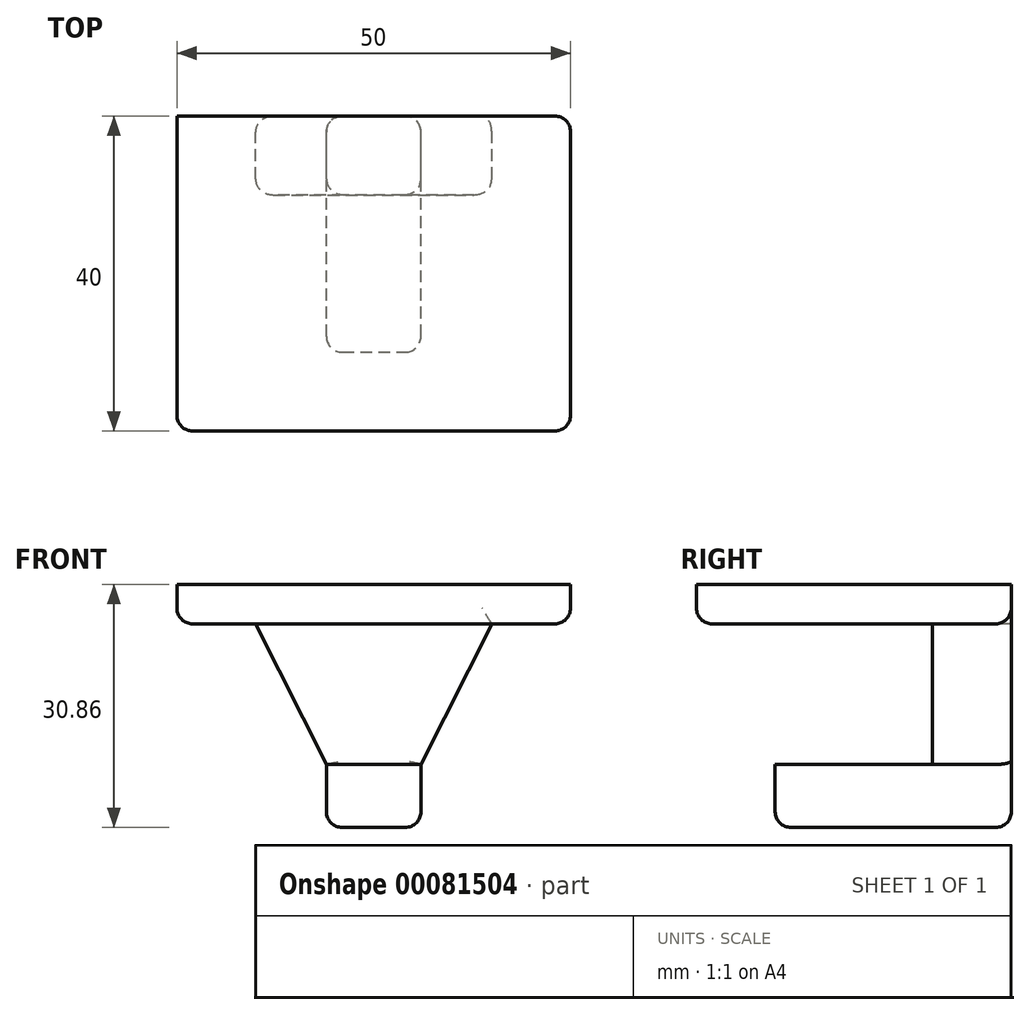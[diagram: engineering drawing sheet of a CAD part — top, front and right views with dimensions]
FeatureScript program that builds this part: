
annotation { "Feature Type Name" : "Feature", "Feature Type Description" : "" }
export const myFeature = defineFeature(function(context is Context, id is Id, definition is map)
    precondition{}
    {
        {
            var Q0;
            Q0=qCreatedBy(makeId("Front.planeOp"),FACE);
            var sketch = newSketch(context, id + "F0", { "sketchPlane" : qUnion([Q0])});
            skLineSegment(sketch, "E0.bottom", {"start": v(-25, 42.41) * mm, "end": v(25, 42.41) * mm});
            skLineSegment(sketch, "E0.top", {"start": v(-25, 37.41) * mm, "end": v(25, 37.41) * mm});
            skLineSegment(sketch, "E0.left", {"start": v(-25, 42.41) * mm, "end": v(-25, 37.41) * mm});
            skLineSegment(sketch, "E0.right", {"start": v(25, 42.41) * mm, "end": v(25, 37.41) * mm});
            skPoint(sketch, "E0.middle", {"position": v(0, 39.91) * mm});
            skLineSegment(sketch, "E1.bottom", {"start": v(-6, 19.55) * mm, "end": v(6, 19.55) * mm});
            skLineSegment(sketch, "E1.top", {"start": v(-6, 11.55) * mm, "end": v(6, 11.55) * mm});
            skLineSegment(sketch, "E1.left", {"start": v(-6, 19.55) * mm, "end": v(-6, 11.55) * mm});
            skLineSegment(sketch, "E1.right", {"start": v(6, 19.55) * mm, "end": v(6, 11.55) * mm});
            skPoint(sketch, "E1.middle", {"position": v(0, 15.55) * mm});
            skLineSegment(sketch, "E2", {"start": v(-15, 37.41) * mm, "end": v(-6, 19.55) * mm});
            skLineSegment(sketch, "E3", {"start": v(15, 37.41) * mm, "end": v(6, 19.55) * mm});
            skSolve(sketch);
        }
        {
            var Q0;
            Q0=makeQuery(id+"F0.imprint","IMPRINT",FACE,{"disambiguationData":[TD([[makeQuery(id+"F0.imprint","IMPRINT",EDGE,{"derivedFrom":sQuery(id+"F0.wireOp",EDGE,"E0.bottom")}),-1.0]])]});
            var Q1;
            Q1=makeQuery(id+"F0.imprint","IMPRINT",FACE,{"disambiguationData":[TD([[makeQuery(id+"F0.imprint","IMPRINT",EDGE,{"derivedFrom":sQuery(id+"F0.wireOp",EDGE,"E1.bottom")}),-1.0]])]});
            extrude(context, id + "F1", {"entities" : qUnion([Q0, Q1]), "depth" : 30 * mm});
        }
        {
            var Q0;
            Q0=makeQuery(id+"F1.opExtrude","CAP_FACE",FACE,{"disambiguationData":[OSD([sQuery(id+"F0.wireOp",EDGE,"E0.bottom"),sQuery(id+"F0.wireOp",EDGE,"E0.top"),sQuery(id+"F0.wireOp",EDGE,"E0.left"),sQuery(id+"F0.wireOp",EDGE,"E0.right")])],"isStart":false});
            extrude(context, id + "F2", {"entities" : qUnion([Q0]), "operationType" : NewBodyOperationType.ADD, "depth" : 10 * mm});
        }
        {
            var Q0;
            Q0=qCreatedBy(makeId("Front.planeOp"),FACE);
            var sketch = newSketch(context, id + "F3", { "sketchPlane" : qUnion([Q0])});
            skLineSegment(sketch, "E4", {"start": v(-6, 19.55) * mm, "end": v(-15, 37.41) * mm});
            skLineSegment(sketch, "E5", {"start": v(-15, 37.41) * mm, "end": v(15, 37.41) * mm});
            skLineSegment(sketch, "E6", {"start": v(15, 37.41) * mm, "end": v(6, 19.55) * mm});
            skLineSegment(sketch, "E7", {"start": v(6, 19.55) * mm, "end": v(-6, 19.55) * mm});
            skSolve(sketch);
        }
        {
            var Q0;
            Q0=sQuery(id+"F3.wireOp",EDGE,"E6");
            var Q1;
            Q1=sQuery(id+"F3.wireOp",EDGE,"E7");
            var Q2;
            Q2=sQuery(id+"F3.wireOp",EDGE,"E5");
            var Q3;
            Q3=sQuery(id+"F3.wireOp",EDGE,"E4");
            extrude(context, id + "F4", {"bodyType" : ToolBodyType.SURFACE, "surfaceEntities" : qUnion([Q0, Q1, Q2, Q3]), "depth" : 10 * mm});
        }
        {
            var Q0;
            Q0 = qSketchRegion(id + "F3", true);
            extrude(context, id + "F5", {"entities" : qUnion([Q0]), "depth" : 10 * mm});
        }
        {
            var Q0;
            {var subQ0=sQuery(id+"F0.wireOp",EDGE,"E0.left");var subQ1=sQuery(id+"F0.wireOp",EDGE,"E0.top");Q0=makeQuery(id+"F2.boolean.opBoolean","MERGE",EDGE,{"derivedFrom":[makeQuery(id+"F1.opExtrude","SWEPT_EDGE",EDGE,{"disambiguationData":[OSD([subQ1,subQ0])]}),makeQuery(id+"F2.opExtrude","SWEPT_EDGE",EDGE,{"disambiguationData":[OSD([subQ1,subQ0])]})]});}
            var Q1;
            Q1=makeQuery(id+"F2.opExtrude","CAP_EDGE",EDGE,{"disambiguationData":[OSD([sQuery(id+"F0.wireOp",EDGE,"E0.top")])],"isStart":false});
            var Q2;
            {var subQ0=sQuery(id+"F0.wireOp",EDGE,"E0.right");var subQ1=sQuery(id+"F0.wireOp",EDGE,"E0.top");Q2=makeQuery(id+"F2.boolean.opBoolean","MERGE",EDGE,{"derivedFrom":[makeQuery(id+"F1.opExtrude","SWEPT_EDGE",EDGE,{"disambiguationData":[OSD([subQ1,subQ0])]}),makeQuery(id+"F2.opExtrude","SWEPT_EDGE",EDGE,{"disambiguationData":[OSD([subQ1,subQ0])]})]});}
            var Q3;
            Q3=makeQuery(id+"F1.opExtrude","CAP_EDGE",EDGE,{"disambiguationData":[OSD([sQuery(id+"F0.wireOp",EDGE,"E1.left")])],"isStart":false});
            var Q4;
            Q4=makeQuery(id+"F1.opExtrude","SWEPT_EDGE",EDGE,{"disambiguationData":[OSD([sQuery(id+"F0.wireOp",EDGE,"E1.top"),sQuery(id+"F0.wireOp",EDGE,"E1.left")])]});
            var Q5;
            Q5=makeQuery(id+"F1.opExtrude","CAP_EDGE",EDGE,{"disambiguationData":[OSD([sQuery(id+"F0.wireOp",EDGE,"E1.top")])],"isStart":false});
            var Q6;
            Q6=makeQuery(id+"F1.opExtrude","SWEPT_EDGE",EDGE,{"disambiguationData":[OSD([sQuery(id+"F0.wireOp",EDGE,"E1.top"),sQuery(id+"F0.wireOp",EDGE,"E1.right")])]});
            var Q7;
            Q7=makeQuery(id+"F1.opExtrude","CAP_EDGE",EDGE,{"disambiguationData":[OSD([sQuery(id+"F0.wireOp",EDGE,"E1.right")])],"isStart":false});
            fillet(context, id + "F6", {"entities" : qUnion([Q0, Q1, Q2, Q3, Q4, Q5, Q6, Q7]), "radius" : 2 * mm, "tangentPropagation" : true, "allowEdgeOverflow" : false});
        }
        {
            var Q0;
            Q0=makeQuery(id+"F5.opExtrude","SWEPT_BODY",BODY,{"disambiguationData":[OSD([sQuery(id+"F3.wireOp",EDGE,"E4"),sQuery(id+"F3.wireOp",EDGE,"E5"),sQuery(id+"F3.wireOp",EDGE,"E6"),sQuery(id+"F3.wireOp",EDGE,"E7")])]});
            var Q1;
            Q1=makeQuery(id+"F1.opExtrude","SWEPT_BODY",BODY,{"disambiguationData":[OSD([sQuery(id+"F0.wireOp",EDGE,"E1.bottom"),sQuery(id+"F0.wireOp",EDGE,"E1.top"),sQuery(id+"F0.wireOp",EDGE,"E1.left"),sQuery(id+"F0.wireOp",EDGE,"E1.right")])]});
            var Q2;
            Q2=makeQuery(id+"F1.opExtrude","SWEPT_BODY",BODY,{"disambiguationData":[OSD([sQuery(id+"F0.wireOp",EDGE,"E0.bottom"),sQuery(id+"F0.wireOp",EDGE,"E0.top"),sQuery(id+"F0.wireOp",EDGE,"E0.left"),sQuery(id+"F0.wireOp",EDGE,"E0.right")])]});
            booleanBodies(context, id + "F7", {"operationType" : BooleanOperationType.UNION, "tools" : qUnion([Q0, Q1, Q2])});
        }
        {
            var Q0;
            Q0=makeQuery(id+"F2.opExtrude","CAP_EDGE",EDGE,{"disambiguationData":[OSD([sQuery(id+"F0.wireOp",EDGE,"E0.left")])],"isStart":false});
            var Q1;
            Q1=makeQuery(id+"F2.opExtrude","CAP_EDGE",EDGE,{"disambiguationData":[OSD([sQuery(id+"F0.wireOp",EDGE,"E0.right")])],"isStart":false});
            var Q2;
            Q2=makeQuery(id+"F5.opExtrude","SWEPT_EDGE",EDGE,{"disambiguationData":[OSD([sQuery(id+"F3.wireOp",EDGE,"E4"),sQuery(id+"F3.wireOp",EDGE,"E5")])]});
            var Q3;
            Q3=makeQuery(id+"F5.opExtrude","CAP_EDGE",EDGE,{"disambiguationData":[OSD([sQuery(id+"F3.wireOp",EDGE,"E5")])],"isStart":false});
            var Q4;
            Q4=makeQuery(id+"F5.opExtrude","CAP_EDGE",EDGE,{"disambiguationData":[OSD([sQuery(id+"F3.wireOp",EDGE,"E4")])],"isStart":false});
            var Q5;
            Q5=makeQuery(id+"F5.opExtrude","CAP_EDGE",EDGE,{"disambiguationData":[OSD([sQuery(id+"F3.wireOp",EDGE,"E4")])],"isStart":true});
            var Q6;
            {var subQ0=sQuery(id+"F0.wireOp",EDGE,"E0.top");var subQ2=sQuery(id+"F3.wireOp",EDGE,"E6");Q6=makeQuery(id+"F7.opBoolean","SPLIT",EDGE,{"disambiguationData":[TD([makeQuery(id+"F5.opExtrude","SWEPT_FACE",FACE,{"disambiguationData":[OSD([subQ2])]})])],"derivedFrom":makeQuery(id+"F1.opExtrude","CAP_EDGE",EDGE,{"disambiguationData":[OSD([subQ0])],"isStart":true})});}
            var Q7;
            Q7=makeQuery(id+"F5.opExtrude","CAP_EDGE",EDGE,{"disambiguationData":[OSD([sQuery(id+"F3.wireOp",EDGE,"E6")])],"isStart":true});
            var Q8;
            Q8=makeQuery(id+"F1.opExtrude","CAP_EDGE",EDGE,{"disambiguationData":[OSD([sQuery(id+"F0.wireOp",EDGE,"E1.top")])],"isStart":true});
            var Q9;
            Q9=makeQuery(id+"F5.opExtrude","CAP_EDGE",EDGE,{"disambiguationData":[OSD([sQuery(id+"F3.wireOp",EDGE,"E6")])],"isStart":false});
            fillet(context, id + "F8", {"entities" : qUnion([Q0, Q1, Q2, Q3, Q4, Q5, Q6, Q7, Q8, Q9]), "radius" : 2 * mm, "tangentPropagation" : true, "allowEdgeOverflow" : false});
        }
    });
